# Revit family: QF_COMCATER ALL BRANDS_RCR6-4
name_source: partatom
category: Specialty Equipment
revit_build: Autodesk Revit 2014 (Build: 20140709_2115(x64)
units: mm (PartAtom-declared; Revit-internal decimal feet)

## types (1)
- RCR6-4_Natural Gas
    Accessory = No
    Assembly Code = E1090320
    BTUH = 28900 W
    Depth Actual = 830 mm  [stored 2.7231 ft]
    Description = 4 BURNER RANGE WITH OVEN
    Gas Flow = 0.0 L/s
    Gas Size = 19 mm
    Gas Size Flexible = 0 mm
    Gas power kW = 28.9
    Height Actual = 1135 mm  [stored 3.72375 ft]
    Length Actual = 600 mm  [stored 1.9685 ft]
    Manufacturer = TRUEHEAT
    Model = RCR6-4
    Nominal Gas power = 28900 W
    Type Comments = The Australian owned and designed* Trueheat RC Series of Gas Cooking Equipment has been developed for the restaurant and cafe market with a high quality finish, designed to fulfill the busy demands within a commercial kitchen.
Powerful 24MJ/hr open burners with individual standing pilots included.
100% Flame failure controls included as standard. Matt finish premium look cast iron trivets radiant heat and design makes it easy to move pots around the surface.
25MJ/hr static oven with two oven racks fit to removable vertical rack guides which provide 3 rack heights. Oven racks are fabricated from 304 stainless steel. Interior oven panels are coated with black vitreous enamel for ease of cleaning.

note: [stored X ft] marks values corroborated as IEEE doubles in the binary element streams (Revit-internal decimal feet)

## geometry (parser evidence)
native form markers: Sweep x7
no freeform markers — native parametric forms only
